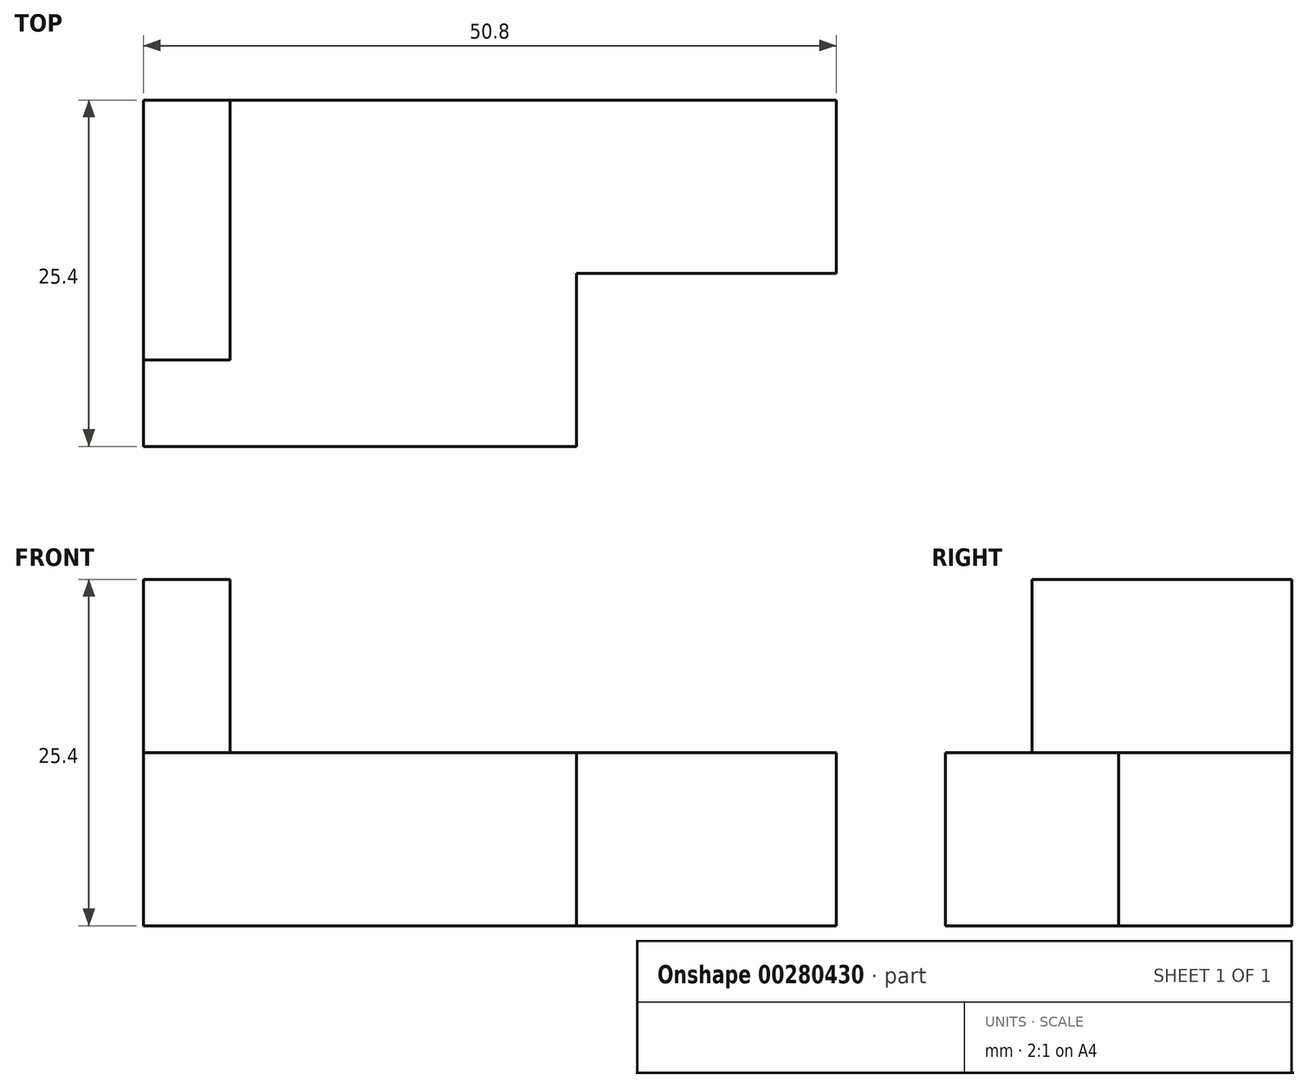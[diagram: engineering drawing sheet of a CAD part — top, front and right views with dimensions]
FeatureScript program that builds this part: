
annotation { "Feature Type Name" : "Feature", "Feature Type Description" : "" }
export const myFeature = defineFeature(function(context is Context, id is Id, definition is map)
    precondition{}
    {
        {
            var Q0;
            Q0=qCreatedBy(makeId("Front.planeOp"),FACE);
            var sketch = newSketch(context, id + "F0", { "sketchPlane" : qUnion([Q0])});
            skLineSegment(sketch, "E0", {"start": v(0, 0) * mm, "end": v(50.8, 0) * mm});
            skLineSegment(sketch, "E1", {"start": v(50.8, 0) * mm, "end": v(50.8, 12.7) * mm});
            skLineSegment(sketch, "E2", {"start": v(50.8, 12.7) * mm, "end": v(6.35, 12.7) * mm});
            skLineSegment(sketch, "E3", {"start": v(6.35, 12.7) * mm, "end": v(6.35, 25.4) * mm});
            skLineSegment(sketch, "E4", {"start": v(6.35, 25.4) * mm, "end": v(0, 25.4) * mm});
            skLineSegment(sketch, "E5", {"start": v(0, 25.4) * mm, "end": v(0, 0) * mm});
            skSolve(sketch);
        }
        {
            var Q0;
            Q0 = qSketchRegion(id + "F0", true);
            extrude(context, id + "F1", {"entities" : qUnion([Q0]), "depth" : 25.4 * mm});
        }
        {
            var Q0;
            Q0=makeQuery(id+"F1.opExtrude","SWEPT_FACE",FACE,{"disambiguationData":[OSD([sQuery(id+"F0.wireOp",EDGE,"E3")])]});
            var sketch = newSketch(context, id + "F2", { "sketchPlane" : qUnion([Q0])});
            skLineSegment(sketch, "E6", {"start": v(-19.05, 25.4) * mm, "end": v(-19.05, 12.7) * mm});
            skLineSegment(sketch, "E7", {"start": v(-19.05, 12.7) * mm, "end": v(-25.4, 12.7) * mm});
            skLineSegment(sketch, "E8", {"start": v(-25.4, 12.7) * mm, "end": v(-25.4, 25.4) * mm});
            skLineSegment(sketch, "E9", {"start": v(-25.4, 25.4) * mm, "end": v(-19.05, 25.4) * mm});
            skSolve(sketch);
        }
        {
            var Q0;
            Q0=makeQuery(id+"F2.imprint","IMPRINT",FACE,{"disambiguationData":[TD([[makeQuery(id+"F2.imprint","IMPRINT",EDGE,{"derivedFrom":sQuery(id+"F2.wireOp",EDGE,"E6")}),-1.0]])]});
            extrude(context, id + "F3", {"entities" : qUnion([Q0]), "operationType" : NewBodyOperationType.REMOVE, "endBound" : BoundingType.THROUGH_ALL, "oppositeDirection" : true, "depth" : 25.4 * mm});
        }
        {
            var Q0;
            Q0=makeQuery(id+"F3.boolean.opBoolean","MERGE",FACE,{"derivedFrom":[makeQuery(id+"F1.opExtrude","SWEPT_FACE",FACE,{"disambiguationData":[OSD([sQuery(id+"F0.wireOp",EDGE,"E2")])]}),makeQuery(id+"F3.opExtrude","SWEPT_FACE",FACE,{"disambiguationData":[OSD([sQuery(id+"F2.wireOp",EDGE,"E7")])]})]});
            var sketch = newSketch(context, id + "F4", { "sketchPlane" : qUnion([Q0])});
            skLineSegment(sketch, "E10", {"start": v(50.8, -12.7) * mm, "end": v(31.75, -12.7) * mm});
            skLineSegment(sketch, "E11", {"start": v(31.75, -12.7) * mm, "end": v(31.75, -25.4) * mm});
            skLineSegment(sketch, "E12", {"start": v(31.75, -25.4) * mm, "end": v(50.8, -25.4) * mm});
            skLineSegment(sketch, "E13", {"start": v(50.8, -25.4) * mm, "end": v(50.8, -12.7) * mm});
            skSolve(sketch);
        }
        {
            var Q0;
            Q0 = qSketchRegion(id + "F4", true);
            extrude(context, id + "F5", {"entities" : qUnion([Q0]), "operationType" : NewBodyOperationType.REMOVE, "endBound" : BoundingType.THROUGH_ALL, "oppositeDirection" : true, "depth" : 25.4 * mm});
        }
    });
